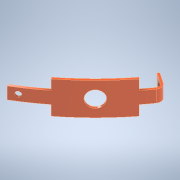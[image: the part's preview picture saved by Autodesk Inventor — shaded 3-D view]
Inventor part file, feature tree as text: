
AUTODESK INVENTOR PART (.ipt)
format: ipt  version: 2021 (Build 250183000, 183)  size: 207,872 bytes
history: native  units: in
note: dims shown in document units (in); Inventor stores cm internally (conversion verified against a paired STEP export)
features: other x5, sketch x4, extrude x1, plane x1
ambient origin geometry x8: Origin, YZ Plane, XZ Plane, XY Plane, X Axis, Y Axis, Z Axis, Center Point
bodies: Solid1 (feature_tree)
feature tree (11):
  extrude  "Extrusion1"  Depth=1.151in
  other  "Bend Part1"
  other  "Bend Part2"
  other  "Work Axis1"
  other  "Work Axis2"
  plane  "Work Plane1"
  sketch  "Sketch4"  dims[d6=0.0926in d8=0.11in d9=0.11in d10=0.0924in d11=0.218in d12=0.051in d13=0.055in d14=0.055in d15=0.051in d16=0.218in d17=0.1475in d18=0.148in d19=0.5755in d20=0.02in d21=0.0in d22=0.0394in d23=90.0deg d24=0.571in d25=0.2855in d26=2.36in d27=360.0deg d28=0.148in d29=0.15in d30=0.75in d31=0.625in d32=0.7in]
  other  "Work Axis3"
  sketch  "Sketch1"  dims[d2=0.295in d3=1.151in]
  sketch  "Sketch2"  dims[d4=0.29in]
  sketch  "Sketch3"  dims[d5=0.29in]
